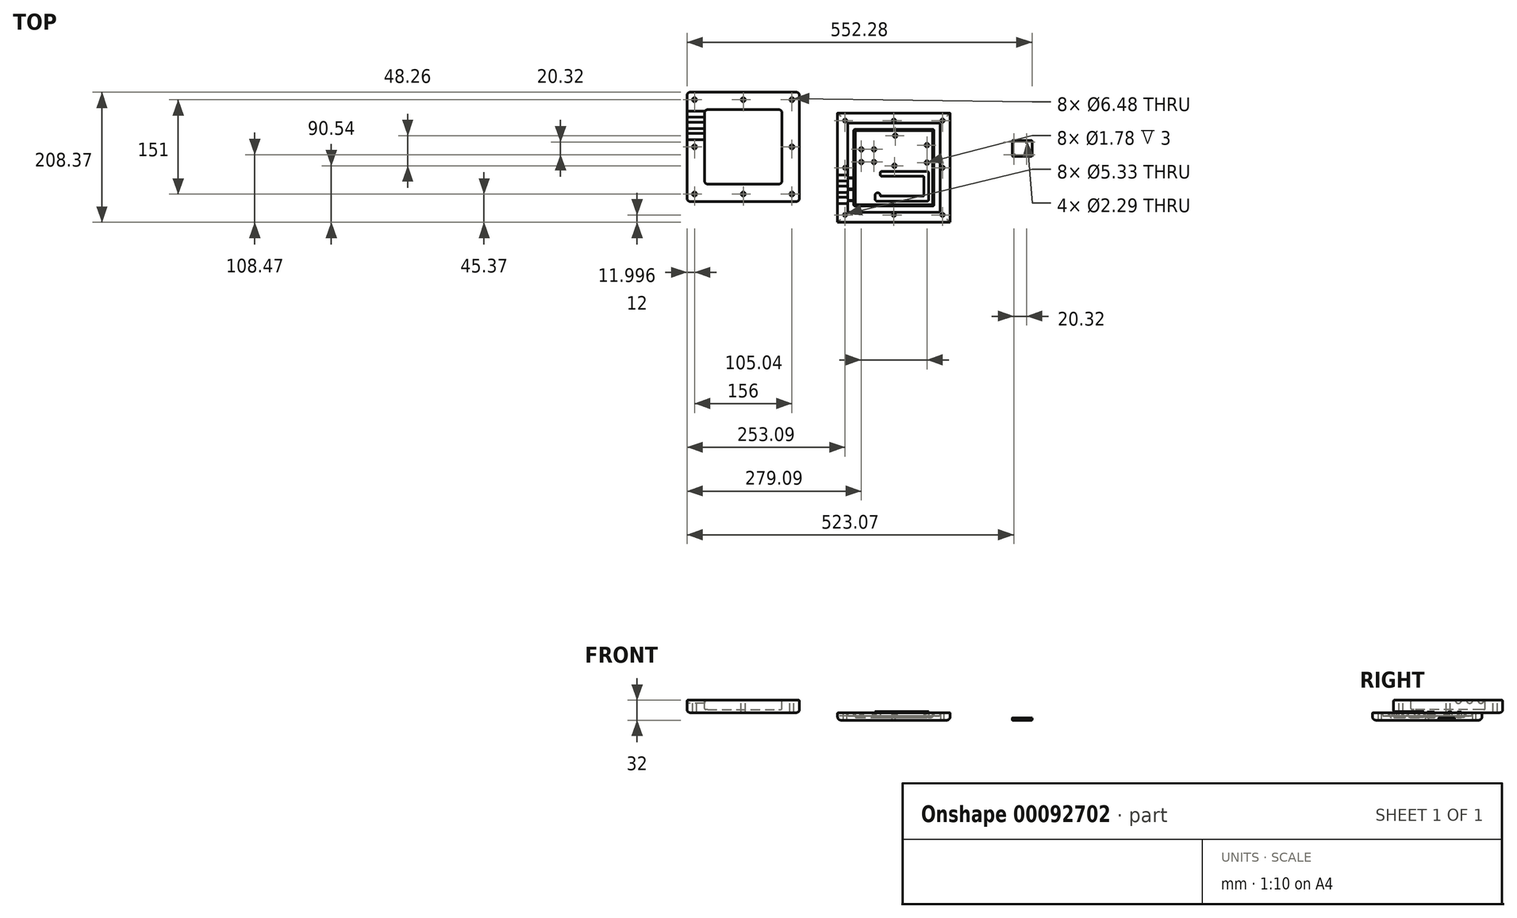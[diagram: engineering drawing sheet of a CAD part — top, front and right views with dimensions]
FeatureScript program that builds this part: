
annotation { "Feature Type Name" : "Feature", "Feature Type Description" : "" }
export const myFeature = defineFeature(function(context is Context, id is Id, definition is map)
    precondition{}
    {
        {
            var Q0;
            Q0=qCreatedBy(makeId("Top.planeOp"),FACE);
            var sketch = newSketch(context, id + "F0", { "sketchPlane" : qUnion([Q0])});
            skLineSegment(sketch, "E0.bottom", {"start": v(-90, 87.5) * mm, "end": v(90, 87.5) * mm});
            skLineSegment(sketch, "E0.top", {"start": v(-90, -87.5) * mm, "end": v(90, -87.5) * mm});
            skLineSegment(sketch, "E0.left", {"start": v(-90, 87.5) * mm, "end": v(-90, -87.5) * mm});
            skLineSegment(sketch, "E0.right", {"start": v(90, 87.5) * mm, "end": v(90, -87.5) * mm});
            skLineSegment(sketch, "E1", {"start": v(0, 87.5) * mm, "end": v(0, 0) * mm});
            skLineSegment(sketch, "E2", {"start": v(0, 0) * mm, "end": v(-90, 0) * mm});
            skSolve(sketch);
        }
        {
            var Q0;
            Q0 = qSketchRegion(id + "F0", true);
            extrude(context, id + "F1", {"entities" : qUnion([Q0]), "depth" : 12 * mm});
        }
        {
            var Q0;
            Q0=makeQuery(id+"F1.opExtrude","CAP_EDGE",EDGE,{"disambiguationData":[OSD([sQuery(id+"F0.wireOp",EDGE,"E0.top")])],"isStart":true});
            var Q1;
            Q1=makeQuery(id+"F1.opExtrude","CAP_EDGE",EDGE,{"disambiguationData":[OSD([sQuery(id+"F0.wireOp",EDGE,"E0.left")])],"isStart":true});
            var Q2;
            Q2=makeQuery(id+"F1.opExtrude","CAP_EDGE",EDGE,{"disambiguationData":[OSD([sQuery(id+"F0.wireOp",EDGE,"E0.bottom")])],"isStart":true});
            var Q3;
            Q3=makeQuery(id+"F1.opExtrude","CAP_EDGE",EDGE,{"disambiguationData":[OSD([sQuery(id+"F0.wireOp",EDGE,"E0.right")])],"isStart":true});
            fillet(context, id + "F2", {"entities" : qUnion([Q0, Q1, Q2, Q3]), "radius" : 5 * mm, "tangentPropagation" : true, "allowEdgeOverflow" : false});
        }
        {
            var Q0;
            Q0=makeQuery(id+"F1.opExtrude","CAP_FACE",FACE,{"disambiguationData":[OSD([sQuery(id+"F0.wireOp",EDGE,"E0.bottom"),sQuery(id+"F0.wireOp",EDGE,"E0.top"),sQuery(id+"F0.wireOp",EDGE,"E0.left"),sQuery(id+"F0.wireOp",EDGE,"E0.right")])],"isStart":false});
            var sketch = newSketch(context, id + "F3", { "sketchPlane" : qUnion([Q0])});
            skLineSegment(sketch, "E3.bottom", {"start": v(-62, 59.5) * mm, "end": v(62, 59.5) * mm});
            skLineSegment(sketch, "E3.top", {"start": v(-62, -59.5) * mm, "end": v(62, -59.5) * mm});
            skLineSegment(sketch, "E3.left", {"start": v(-62, 59.5) * mm, "end": v(-62, -59.5) * mm});
            skLineSegment(sketch, "E3.right", {"start": v(62, 59.5) * mm, "end": v(62, -59.5) * mm});
            skLineSegment(sketch, "E4", {"start": v(0, 59.5) * mm, "end": v(0, 0) * mm});
            skLineSegment(sketch, "E5", {"start": v(0, 0) * mm, "end": v(-62, 0) * mm});
            skSolve(sketch);
        }
        {
            var Q0;
            Q0 = qSketchRegion(id + "F3", true);
            extrude(context, id + "F4", {"entities" : qUnion([Q0]), "operationType" : NewBodyOperationType.REMOVE, "oppositeDirection" : true, "depth" : 8 * mm});
        }
        {
            var Q0;
            Q0=makeQuery(id+"F4.boolean.opBoolean","COPY",EDGE,{"derivedFrom":makeQuery(id+"F4.opExtrude","CAP_EDGE",EDGE,{"disambiguationData":[OSD([sQuery(id+"F3.wireOp",EDGE,"E3.bottom")])],"isStart":false})});
            var Q1;
            Q1=makeQuery(id+"F4.boolean.opBoolean","COPY",EDGE,{"derivedFrom":makeQuery(id+"F4.opExtrude","CAP_EDGE",EDGE,{"disambiguationData":[OSD([sQuery(id+"F3.wireOp",EDGE,"E3.right")])],"isStart":false})});
            var Q2;
            Q2=makeQuery(id+"F4.boolean.opBoolean","COPY",EDGE,{"derivedFrom":makeQuery(id+"F4.opExtrude","CAP_EDGE",EDGE,{"disambiguationData":[OSD([sQuery(id+"F3.wireOp",EDGE,"E3.top")])],"isStart":false})});
            var Q3;
            Q3=makeQuery(id+"F4.boolean.opBoolean","COPY",EDGE,{"derivedFrom":makeQuery(id+"F4.opExtrude","CAP_EDGE",EDGE,{"disambiguationData":[OSD([sQuery(id+"F3.wireOp",EDGE,"E3.left")])],"isStart":false})});
            fillet(context, id + "F5", {"entities" : qUnion([Q0, Q1, Q2, Q3]), "radius" : 2 * mm, "tangentPropagation" : true, "allowEdgeOverflow" : false});
        }
        {
            var Q0;
            Q0=makeQuery(id+"F1.opExtrude","CAP_EDGE",EDGE,{"disambiguationData":[OSD([sQuery(id+"F0.wireOp",EDGE,"E0.top")])],"isStart":false});
            var Q1;
            Q1=makeQuery(id+"F1.opExtrude","CAP_EDGE",EDGE,{"disambiguationData":[OSD([sQuery(id+"F0.wireOp",EDGE,"E0.left")])],"isStart":false});
            var Q2;
            Q2=makeQuery(id+"F1.opExtrude","CAP_EDGE",EDGE,{"disambiguationData":[OSD([sQuery(id+"F0.wireOp",EDGE,"E0.bottom")])],"isStart":false});
            var Q3;
            Q3=makeQuery(id+"F1.opExtrude","CAP_EDGE",EDGE,{"disambiguationData":[OSD([sQuery(id+"F0.wireOp",EDGE,"E0.right")])],"isStart":false});
            fillet(context, id + "F6", {"entities" : qUnion([Q0, Q1, Q2, Q3]), "radius" : 1 * mm, "tangentPropagation" : true, "allowEdgeOverflow" : false});
        }
        {
            var Q0;
            Q0=makeQuery(id+"F1.opExtrude","CAP_FACE",FACE,{"disambiguationData":[OSD([sQuery(id+"F0.wireOp",EDGE,"E0.bottom"),sQuery(id+"F0.wireOp",EDGE,"E0.top"),sQuery(id+"F0.wireOp",EDGE,"E0.left"),sQuery(id+"F0.wireOp",EDGE,"E0.right")])],"isStart":false});
            var sketch = newSketch(context, id + "F7", { "sketchPlane" : qUnion([Q0])});
            skLineSegment(sketch, "E6.bottom", {"start": v(-64, 61.5) * mm, "end": v(64, 61.5) * mm});
            skLineSegment(sketch, "E6.top", {"start": v(-64, -61.5) * mm, "end": v(64, -61.5) * mm});
            skLineSegment(sketch, "E6.left", {"start": v(-64, 61.5) * mm, "end": v(-64, -61.5) * mm});
            skLineSegment(sketch, "E6.right", {"start": v(64, 61.5) * mm, "end": v(64, -61.5) * mm});
            skLineSegment(sketch, "E7", {"start": v(-64, 0) * mm, "end": v(0, 0) * mm, "construction": true});
            skLineSegment(sketch, "E8", {"start": v(0, 0) * mm, "end": v(0, 61.5) * mm, "construction": true});
            skLineSegment(sketch, "E9.bottom", {"start": v(-74, 71.5) * mm, "end": v(74, 71.5) * mm});
            skLineSegment(sketch, "E9.top", {"start": v(-74, -71.5) * mm, "end": v(74, -71.5) * mm});
            skLineSegment(sketch, "E9.left", {"start": v(-74, 71.5) * mm, "end": v(-74, -71.5) * mm});
            skLineSegment(sketch, "E9.right", {"start": v(74, 71.5) * mm, "end": v(74, -71.5) * mm});
            skLineSegment(sketch, "E10", {"start": v(0, 61.5) * mm, "end": v(0, 71.5) * mm, "construction": true});
            skPoint(sketch, "E10.startSnap0", {"position": v(0, 71.5) * mm});
            skLineSegment(sketch, "E11", {"start": v(-64, 0) * mm, "end": v(-74, 0) * mm, "construction": true});
            skSolve(sketch);
        }
        {
            var Q0;
            Q0=makeQuery(id+"F7.imprint","IMPRINT",FACE,{"disambiguationData":[TD([[makeQuery(id+"F7.imprint","IMPRINT",EDGE,{"derivedFrom":sQuery(id+"F7.wireOp",EDGE,"E6.bottom")}),1.0]])]});
            extrude(context, id + "F8", {"entities" : qUnion([Q0]), "operationType" : NewBodyOperationType.REMOVE, "oppositeDirection" : true, "depth" : 5 * mm});
        }
        {
            var Q0;
            Q0=makeQuery(id+"F8.boolean.opBoolean","COPY",EDGE,{"derivedFrom":makeQuery(id+"F8.opExtrude","SWEPT_EDGE",EDGE,{"disambiguationData":[OSD([sQuery(id+"F7.wireOp",EDGE,"E9.bottom"),sQuery(id+"F7.wireOp",EDGE,"E9.left")])]})});
            var Q1;
            Q1=makeQuery(id+"F8.boolean.opBoolean","COPY",EDGE,{"derivedFrom":makeQuery(id+"F8.opExtrude","SWEPT_EDGE",EDGE,{"disambiguationData":[OSD([sQuery(id+"F7.wireOp",EDGE,"E9.bottom"),sQuery(id+"F7.wireOp",EDGE,"E9.right")])]})});
            var Q2;
            Q2=makeQuery(id+"F8.boolean.opBoolean","COPY",EDGE,{"derivedFrom":makeQuery(id+"F8.opExtrude","SWEPT_EDGE",EDGE,{"disambiguationData":[OSD([sQuery(id+"F7.wireOp",EDGE,"E9.top"),sQuery(id+"F7.wireOp",EDGE,"E9.right")])]})});
            var Q3;
            Q3=makeQuery(id+"F8.boolean.opBoolean","COPY",EDGE,{"derivedFrom":makeQuery(id+"F8.opExtrude","SWEPT_EDGE",EDGE,{"disambiguationData":[OSD([sQuery(id+"F7.wireOp",EDGE,"E9.top"),sQuery(id+"F7.wireOp",EDGE,"E9.left")])]})});
            var Q4;
            Q4=makeQuery(id+"F8.boolean.opBoolean","COPY",EDGE,{"derivedFrom":makeQuery(id+"F8.opExtrude","SWEPT_EDGE",EDGE,{"disambiguationData":[OSD([sQuery(id+"F7.wireOp",EDGE,"E6.bottom"),sQuery(id+"F7.wireOp",EDGE,"E6.right")])]})});
            var Q5;
            Q5=makeQuery(id+"F8.boolean.opBoolean","COPY",EDGE,{"derivedFrom":makeQuery(id+"F8.opExtrude","SWEPT_EDGE",EDGE,{"disambiguationData":[OSD([sQuery(id+"F7.wireOp",EDGE,"E6.bottom"),sQuery(id+"F7.wireOp",EDGE,"E6.left")])]})});
            var Q6;
            Q6=makeQuery(id+"F8.boolean.opBoolean","COPY",EDGE,{"derivedFrom":makeQuery(id+"F8.opExtrude","SWEPT_EDGE",EDGE,{"disambiguationData":[OSD([sQuery(id+"F7.wireOp",EDGE,"E6.top"),sQuery(id+"F7.wireOp",EDGE,"E6.left")])]})});
            var Q7;
            Q7=makeQuery(id+"F8.boolean.opBoolean","COPY",EDGE,{"derivedFrom":makeQuery(id+"F8.opExtrude","SWEPT_EDGE",EDGE,{"disambiguationData":[OSD([sQuery(id+"F7.wireOp",EDGE,"E6.top"),sQuery(id+"F7.wireOp",EDGE,"E6.right")])]})});
            fillet(context, id + "F9", {"entities" : qUnion([Q0, Q1, Q2, Q3, Q4, Q5, Q6, Q7]), "radius" : 2 * mm, "tangentPropagation" : true, "allowEdgeOverflow" : false});
        }
        {
            var Q0;
            Q0=makeQuery(id+"F8.boolean.opBoolean","COPY",EDGE,{"derivedFrom":makeQuery(id+"F8.opExtrude","CAP_EDGE",EDGE,{"disambiguationData":[OSD([sQuery(id+"F7.wireOp",EDGE,"E9.bottom")])],"isStart":false})});
            var Q1;
            Q1=makeQuery(id+"F8.boolean.opBoolean","COPY",EDGE,{"derivedFrom":makeQuery(id+"F8.opExtrude","CAP_EDGE",EDGE,{"disambiguationData":[OSD([sQuery(id+"F7.wireOp",EDGE,"E6.right")])],"isStart":false})});
            fillet(context, id + "F10", {"entities" : qUnion([Q0, Q1]), "radius" : 2 * mm, "tangentPropagation" : true, "allowEdgeOverflow" : false});
        }
        {
            var Q0;
            Q0=makeQuery(id+"F8.boolean.opBoolean","COPY",FACE,{"derivedFrom":makeQuery(id+"F8.opExtrude","CAP_FACE",FACE,{"disambiguationData":[OSD([sQuery(id+"F7.wireOp",EDGE,"E6.bottom"),sQuery(id+"F7.wireOp",EDGE,"E6.top"),sQuery(id+"F7.wireOp",EDGE,"E6.left"),sQuery(id+"F7.wireOp",EDGE,"E6.right"),sQuery(id+"F7.wireOp",EDGE,"E9.bottom"),sQuery(id+"F7.wireOp",EDGE,"E9.top"),sQuery(id+"F7.wireOp",EDGE,"E9.left"),sQuery(id+"F7.wireOp",EDGE,"E9.right")])],"isStart":false})});
            var sketch = newSketch(context, id + "F11", { "sketchPlane" : qUnion([Q0])});
            skLineSegment(sketch, "E12.bottom", {"start": v(-71.5, 71) * mm, "end": v(71.5, 71) * mm});
            skLineSegment(sketch, "E12.top", {"start": v(-71.5, -71) * mm, "end": v(71.5, -71) * mm});
            skLineSegment(sketch, "E12.left", {"start": v(-73.5, 69) * mm, "end": v(-73.5, -69) * mm});
            skLineSegment(sketch, "E12.right", {"start": v(73.5, 69) * mm, "end": v(73.5, -69) * mm});
            skLineSegment(sketch, "E13.bottom", {"start": v(-62.37, 61.87) * mm, "end": v(62.37, 61.87) * mm});
            skLineSegment(sketch, "E13.top", {"start": v(-62.37, -61.87) * mm, "end": v(62.37, -61.87) * mm});
            skLineSegment(sketch, "E13.left", {"start": v(-64.37, 59.87) * mm, "end": v(-64.37, -59.87) * mm});
            skLineSegment(sketch, "E13.right", {"start": v(64.37, 59.87) * mm, "end": v(64.37, -59.87) * mm});
            skLineSegment(sketch, "E14", {"start": v(0, 61.87) * mm, "end": v(0, 71) * mm, "construction": true});
            skLineSegment(sketch, "E15", {"start": v(-64.37, 0) * mm, "end": v(-73.5, 0) * mm, "construction": true});
            skPoint(sketch, "E16", {"position": v(-72, 0) * mm});
            skPoint(sketch, "E17.visualSharp", {"position": v(-73.5, 71) * mm});
            skArc(sketch, "E17.filletArc", {"start": v(-71.5, 71) * mm, "mid": v(-72.91, 70.41) * mm, "end": v(-73.5, 69) * mm});
            skPoint(sketch, "E18.visualSharp", {"position": v(73.5, 71) * mm});
            skArc(sketch, "E18.filletArc", {"start": v(73.5, 69) * mm, "mid": v(72.91, 70.41) * mm, "end": v(71.5, 71) * mm});
            skPoint(sketch, "E19.visualSharp", {"position": v(73.5, -71) * mm});
            skArc(sketch, "E19.filletArc", {"start": v(71.5, -71) * mm, "mid": v(72.91, -70.41) * mm, "end": v(73.5, -69) * mm});
            skPoint(sketch, "E20.visualSharp", {"position": v(-73.5, -71) * mm});
            skArc(sketch, "E20.filletArc", {"start": v(-73.5, -69) * mm, "mid": v(-72.91, -70.41) * mm, "end": v(-71.5, -71) * mm});
            skPoint(sketch, "E21.visualSharp", {"position": v(-64.37, -61.87) * mm});
            skArc(sketch, "E21.filletArc", {"start": v(-64.37, -59.87) * mm, "mid": v(-63.79, -61.29) * mm, "end": v(-62.37, -61.87) * mm});
            skPoint(sketch, "E22.visualSharp", {"position": v(64.37, -61.87) * mm});
            skArc(sketch, "E22.filletArc", {"start": v(62.37, -61.87) * mm, "mid": v(63.79, -61.29) * mm, "end": v(64.37, -59.87) * mm});
            skPoint(sketch, "E23.visualSharp", {"position": v(64.37, 61.87) * mm});
            skArc(sketch, "E23.filletArc", {"start": v(64.37, 59.87) * mm, "mid": v(63.79, 61.29) * mm, "end": v(62.37, 61.87) * mm});
            skPoint(sketch, "E24.visualSharp", {"position": v(-64.37, 61.87) * mm});
            skArc(sketch, "E24.filletArc", {"start": v(-62.37, 61.87) * mm, "mid": v(-63.79, 61.29) * mm, "end": v(-64.37, 59.87) * mm});
            skSolve(sketch);
        }
        {
            var Q0;
            Q0 = qSketchRegion(id + "F11", true);
            extrude(context, id + "F12", {"entities" : qUnion([Q0]), "depth" : 5 / 406.4 * mm});
        }
        {
            var Q0;
            Q0=makeQuery(id+"F12.opExtrude","CAP_EDGE",EDGE,{"disambiguationData":[OSD([sQuery(id+"F11.wireOp",EDGE,"E12.left")])],"isStart":false});
            var Q1;
            Q1=makeQuery(id+"F12.opExtrude","CAP_EDGE",EDGE,{"disambiguationData":[OSD([sQuery(id+"F11.wireOp",EDGE,"E13.left")])],"isStart":false});
            fillet(context, id + "F13", {"entities" : qUnion([Q0, Q1]), "radius" : 4 * mm, "tangentPropagation" : true, "allowEdgeOverflow" : false});
        }
        {
            var Q0;
            Q0=makeQuery(id+"F4.boolean.opBoolean","COPY",FACE,{"derivedFrom":makeQuery(id+"F4.opExtrude","CAP_FACE",FACE,{"disambiguationData":[OSD([sQuery(id+"F3.wireOp",EDGE,"E3.bottom"),sQuery(id+"F3.wireOp",EDGE,"E3.top"),sQuery(id+"F3.wireOp",EDGE,"E3.left"),sQuery(id+"F3.wireOp",EDGE,"E3.right")])],"isStart":false})});
            var sketch = newSketch(context, id + "F14", { "sketchPlane" : qUnion([Q0])});
            skLineSegment(sketch, "E25.bottom", {"start": v(-13, 53.5) * mm, "end": v(56, 53.5) * mm, "construction": true});
            skLineSegment(sketch, "E25.top", {"start": v(-13, 0.5) * mm, "end": v(56, 0.5) * mm, "construction": true});
            skLineSegment(sketch, "E25.left", {"start": v(-13, 53.5) * mm, "end": v(-13, 0.5) * mm, "construction": true});
            skLineSegment(sketch, "E25.right", {"start": v(56, 53.5) * mm, "end": v(56, 0.5) * mm, "construction": true});
            skCircle(sketch, "E26", {"center": v(0.97, 3.04) * mm, "radius": 3 * mm});
            skCircle(sketch, "E27", {"center": v(2.24, 51.3) * mm, "radius": 3 * mm});
            skCircle(sketch, "E28", {"center": v(53.04, 36.06) * mm, "radius": 3 * mm});
            skCircle(sketch, "E29", {"center": v(53.04, 8.12) * mm, "radius": 3 * mm});
            skSolve(sketch);
        }
        {
            var Q0;
            Q0 = qSketchRegion(id + "F14", true);
            extrude(context, id + "F15", {"entities" : qUnion([Q0]), "operationType" : NewBodyOperationType.ADD, "depth" : 9 * mm});
        }
        {
            var Q0;
            Q0=makeQuery(id+"F15.opExtrude","CAP_FACE",FACE,{"disambiguationData":[OSD([sQuery(id+"F14.wireOp",EDGE,"E27")])],"isStart":false});
            var sketch = newSketch(context, id + "F16", { "sketchPlane" : qUnion([Q0])});
            skCircle(sketch, "E30", {"center": v(2.24, 51.3) * mm, "radius": 0.89 * mm});
            skCircle(sketch, "E31", {"center": v(53.04, 36.06) * mm, "radius": 0.89 * mm});
            skCircle(sketch, "E32", {"center": v(53.04, 8.12) * mm, "radius": 0.89 * mm});
            skCircle(sketch, "E33", {"center": v(0.97, 3.04) * mm, "radius": 0.89 * mm});
            skSolve(sketch);
        }
        {
            var Q0;
            Q0 = qSketchRegion(id + "F16", true);
            extrude(context, id + "F17", {"entities" : qUnion([Q0]), "operationType" : NewBodyOperationType.REMOVE, "oppositeDirection" : true, "depth" : 3 * mm});
        }
        {
            var Q0;
            Q0=makeQuery(id+"F4.boolean.opBoolean","COPY",FACE,{"derivedFrom":makeQuery(id+"F4.opExtrude","CAP_FACE",FACE,{"disambiguationData":[OSD([sQuery(id+"F3.wireOp",EDGE,"E3.bottom"),sQuery(id+"F3.wireOp",EDGE,"E3.top"),sQuery(id+"F3.wireOp",EDGE,"E3.left"),sQuery(id+"F3.wireOp",EDGE,"E3.right")])],"isStart":false})});
            var sketch = newSketch(context, id + "F18", { "sketchPlane" : qUnion([Q0])});
            skLineSegment(sketch, "E34", {"start": v(-21.85, -5.75) * mm, "end": v(-21.85, -13.75) * mm});
            skLineSegment(sketch, "E35", {"start": v(-21.85, -13.75) * mm, "end": v(48, -13.75) * mm});
            skLineSegment(sketch, "E36", {"start": v(48, -13.75) * mm, "end": v(48, -45.5) * mm});
            skLineSegment(sketch, "E37", {"start": v(48, -45.5) * mm, "end": v(-21.85, -45.5) * mm});
            skLineSegment(sketch, "E38", {"start": v(-21.85, -45.5) * mm, "end": v(-21.85, -40.5) * mm});
            skLineSegment(sketch, "E39", {"start": v(-21.85, -40.5) * mm, "end": v(-29.85, -40.5) * mm});
            skLineSegment(sketch, "E40", {"start": v(-29.85, -40.5) * mm, "end": v(-29.85, -53.5) * mm});
            skLineSegment(sketch, "E41", {"start": v(-29.85, -53.5) * mm, "end": v(56, -53.5) * mm});
            skLineSegment(sketch, "E42", {"start": v(56, -53.5) * mm, "end": v(56, -5.75) * mm});
            skLineSegment(sketch, "E43", {"start": v(56, -5.75) * mm, "end": v(-21.85, -5.75) * mm});
            skSolve(sketch);
        }
        {
            var Q0;
            Q0 = qSketchRegion(id + "F18", true);
            extrude(context, id + "F19", {"entities" : qUnion([Q0]), "operationType" : NewBodyOperationType.ADD, "depth" : 10 * mm});
        }
        {
            var Q0;
            Q0=makeQuery(id+"F19.opExtrude","SWEPT_EDGE",EDGE,{"disambiguationData":[OSD([sQuery(id+"F18.wireOp",EDGE,"E40"),sQuery(id+"F18.wireOp",EDGE,"E41")])]});
            var Q1;
            Q1=makeQuery(id+"F19.opExtrude","SWEPT_EDGE",EDGE,{"disambiguationData":[OSD([sQuery(id+"F18.wireOp",EDGE,"E39"),sQuery(id+"F18.wireOp",EDGE,"E40")])]});
            var Q2;
            Q2=makeQuery(id+"F19.opExtrude","SWEPT_EDGE",EDGE,{"disambiguationData":[OSD([sQuery(id+"F18.wireOp",EDGE,"E38"),sQuery(id+"F18.wireOp",EDGE,"E39")])]});
            var Q3;
            Q3=makeQuery(id+"F19.opExtrude","SWEPT_EDGE",EDGE,{"disambiguationData":[OSD([sQuery(id+"F18.wireOp",EDGE,"E34"),sQuery(id+"F18.wireOp",EDGE,"E43")])]});
            var Q4;
            Q4=makeQuery(id+"F19.opExtrude","SWEPT_EDGE",EDGE,{"disambiguationData":[OSD([sQuery(id+"F18.wireOp",EDGE,"E42"),sQuery(id+"F18.wireOp",EDGE,"E43")])]});
            var Q5;
            Q5=makeQuery(id+"F19.opExtrude","SWEPT_EDGE",EDGE,{"disambiguationData":[OSD([sQuery(id+"F18.wireOp",EDGE,"E41"),sQuery(id+"F18.wireOp",EDGE,"E42")])]});
            var Q6;
            Q6=makeQuery(id+"F19.opExtrude","SWEPT_EDGE",EDGE,{"disambiguationData":[OSD([sQuery(id+"F18.wireOp",EDGE,"E34"),sQuery(id+"F18.wireOp",EDGE,"E35")])]});
            fillet(context, id + "F20", {"entities" : qUnion([Q0, Q1, Q2, Q3, Q4, Q5, Q6]), "radius" : 3 * mm, "tangentPropagation" : true, "allowEdgeOverflow" : false});
        }
        {
            var Q0;
            Q0=makeQuery(id+"F19.opExtrude","SWEPT_EDGE",EDGE,{"disambiguationData":[OSD([sQuery(id+"F18.wireOp",EDGE,"E37"),sQuery(id+"F18.wireOp",EDGE,"E38")])]});
            var Q1;
            Q1=makeQuery(id+"F19.opExtrude","SWEPT_EDGE",EDGE,{"disambiguationData":[OSD([sQuery(id+"F18.wireOp",EDGE,"E36"),sQuery(id+"F18.wireOp",EDGE,"E37")])]});
            var Q2;
            Q2=makeQuery(id+"F19.opExtrude","SWEPT_EDGE",EDGE,{"disambiguationData":[OSD([sQuery(id+"F18.wireOp",EDGE,"E35"),sQuery(id+"F18.wireOp",EDGE,"E36")])]});
            fillet(context, id + "F21", {"entities" : qUnion([Q0, Q1, Q2]), "radius" : 1 * mm, "tangentPropagation" : true, "allowEdgeOverflow" : false});
        }
        {
            var Q0;
            Q0=makeQuery(id+"F19.opExtrude","CAP_EDGE",EDGE,{"disambiguationData":[OSD([sQuery(id+"F18.wireOp",EDGE,"E41")])],"isStart":true});
            var Q1;
            Q1=makeQuery(id+"F19.opExtrude","CAP_EDGE",EDGE,{"disambiguationData":[OSD([sQuery(id+"F18.wireOp",EDGE,"E41")])],"isStart":false});
            fillet(context, id + "F22", {"entities" : qUnion([Q0, Q1]), "radius" : 1 * mm, "tangentPropagation" : true, "allowEdgeOverflow" : false});
        }
        {
            var Q0;
            Q0=qCreatedBy(makeId("Top.planeOp"),FACE);
            var sketch = newSketch(context, id + "F23", { "sketchPlane" : qUnion([Q0])});
            skLineSegment(sketch, "E44.bottom", {"start": v(189.44, 43.83) * mm, "end": v(221.19, 43.83) * mm});
            skLineSegment(sketch, "E44.top", {"start": v(189.44, 18.43) * mm, "end": v(221.19, 18.43) * mm});
            skLineSegment(sketch, "E44.left", {"start": v(189.44, 43.83) * mm, "end": v(189.44, 18.43) * mm});
            skLineSegment(sketch, "E44.right", {"start": v(221.19, 43.83) * mm, "end": v(221.19, 18.43) * mm});
            skCircle(sketch, "E45", {"center": v(191.98, 20.97) * mm, "radius": 1.14 * mm});
            skCircle(sketch, "E46", {"center": v(191.98, 41.3) * mm, "radius": 1.14 * mm});
            skCircle(sketch, "E47", {"center": v(212.3, 41.3) * mm, "radius": 1.14 * mm});
            skCircle(sketch, "E48", {"center": v(212.3, 20.97) * mm, "radius": 1.14 * mm});
            skSolve(sketch);
        }
        {
            var Q0;
            Q0 = qSketchRegion(id + "F23", true);
            extrude(context, id + "F24", {"entities" : qUnion([Q0]), "depth" : 3.75 * mm});
        }
        {
            var Q0;
            Q0=makeQuery(id+"F24.opExtrude","SWEPT_EDGE",EDGE,{"disambiguationData":[OSD([sQuery(id+"F23.wireOp",EDGE,"E44.top"),sQuery(id+"F23.wireOp",EDGE,"E44.left")])]});
            var Q1;
            Q1=makeQuery(id+"F24.opExtrude","SWEPT_EDGE",EDGE,{"disambiguationData":[OSD([sQuery(id+"F23.wireOp",EDGE,"E44.top"),sQuery(id+"F23.wireOp",EDGE,"E44.right")])]});
            var Q2;
            Q2=makeQuery(id+"F24.opExtrude","SWEPT_EDGE",EDGE,{"disambiguationData":[OSD([sQuery(id+"F23.wireOp",EDGE,"E44.bottom"),sQuery(id+"F23.wireOp",EDGE,"E44.right")])]});
            var Q3;
            Q3=makeQuery(id+"F24.opExtrude","SWEPT_EDGE",EDGE,{"disambiguationData":[OSD([sQuery(id+"F23.wireOp",EDGE,"E44.bottom"),sQuery(id+"F23.wireOp",EDGE,"E44.left")])]});
            fillet(context, id + "F25", {"entities" : qUnion([Q0, Q1, Q2, Q3]), "radius" : 1 * mm, "tangentPropagation" : true, "allowEdgeOverflow" : false});
        }
        {
            var Q0;
            Q0=makeQuery(id+"F24.opExtrude","CAP_EDGE",EDGE,{"disambiguationData":[OSD([sQuery(id+"F23.wireOp",EDGE,"E44.bottom")])],"isStart":false});
            var Q1;
            Q1=makeQuery(id+"F24.opExtrude","CAP_EDGE",EDGE,{"disambiguationData":[OSD([sQuery(id+"F23.wireOp",EDGE,"E44.bottom")])],"isStart":true});
            fillet(context, id + "F26", {"entities" : qUnion([Q0, Q1]), "radius" : 0.5 * mm, "tangentPropagation" : true, "allowEdgeOverflow" : false});
        }
        {
            var Q0;
            Q0=makeQuery(id+"F4.boolean.opBoolean","COPY",FACE,{"derivedFrom":makeQuery(id+"F4.opExtrude","CAP_FACE",FACE,{"disambiguationData":[OSD([sQuery(id+"F3.wireOp",EDGE,"E3.bottom"),sQuery(id+"F3.wireOp",EDGE,"E3.top"),sQuery(id+"F3.wireOp",EDGE,"E3.left"),sQuery(id+"F3.wireOp",EDGE,"E3.right")])],"isStart":false})});
            var sketch = newSketch(context, id + "F27", { "sketchPlane" : qUnion([Q0])});
            skCircle(sketch, "E49", {"center": v(-52, 29.5) * mm, "radius": 3 * mm});
            skCircle(sketch, "E50", {"center": v(-31.68, 29.5) * mm, "radius": 3 * mm});
            skCircle(sketch, "E51", {"center": v(-52, 9.18) * mm, "radius": 3 * mm});
            skCircle(sketch, "E52", {"center": v(-31.68, 9.18) * mm, "radius": 3 * mm});
            skSolve(sketch);
        }
        {
            var Q0;
            Q0 = qSketchRegion(id + "F27", true);
            extrude(context, id + "F28", {"entities" : qUnion([Q0]), "operationType" : NewBodyOperationType.ADD, "depth" : 6 * mm});
        }
        {
            var Q0;
            Q0=makeQuery(id+"F28.opExtrude","CAP_FACE",FACE,{"disambiguationData":[OSD([sQuery(id+"F27.wireOp",EDGE,"E49")])],"isStart":false});
            var sketch = newSketch(context, id + "F29", { "sketchPlane" : qUnion([Q0])});
            skCircle(sketch, "E53", {"center": v(-52, 29.5) * mm, "radius": 0.89 * mm});
            skCircle(sketch, "E54", {"center": v(-52, 9.18) * mm, "radius": 0.89 * mm});
            skCircle(sketch, "E55", {"center": v(-31.68, 9.18) * mm, "radius": 0.89 * mm});
            skCircle(sketch, "E56", {"center": v(-31.68, 29.5) * mm, "radius": 0.89 * mm});
            skSolve(sketch);
        }
        {
            var Q0;
            Q0 = qSketchRegion(id + "F29", true);
            extrude(context, id + "F30", {"entities" : qUnion([Q0]), "operationType" : NewBodyOperationType.REMOVE, "oppositeDirection" : true, "depth" : 3 * mm});
        }
        {
            var Q0;
            {var subQ0=sQuery(id+"F0.wireOp",EDGE,"E0.right");var subQ1=sQuery(id+"F0.wireOp",EDGE,"E0.left");var subQ2=sQuery(id+"F0.wireOp",EDGE,"E0.top");var subQ3=sQuery(id+"F0.wireOp",EDGE,"E0.bottom");Q0=makeQuery(id+"F8.boolean.opBoolean","SPLIT",FACE,{"disambiguationData":[TD([makeQuery(id+"F6.opFillet","BLEND_FACE",FACE,{"disambiguationData":[OSD([subQ3])]})])],"derivedFrom":makeQuery(id+"F1.opExtrude","CAP_FACE",FACE,{"disambiguationData":[OSD([subQ3,subQ2,subQ1,subQ0])],"isStart":false})});}
            var sketch = newSketch(context, id + "F31", { "sketchPlane" : qUnion([Q0])});
            skLineSegment(sketch, "E57.bottom", {"start": v(-78, 75.5) * mm, "end": v(78, 75.5) * mm, "construction": true});
            skLineSegment(sketch, "E57.top", {"start": v(-78, -75.5) * mm, "end": v(78, -75.5) * mm, "construction": true});
            skLineSegment(sketch, "E57.left", {"start": v(-78, 75.5) * mm, "end": v(-78, -75.5) * mm, "construction": true});
            skLineSegment(sketch, "E57.right", {"start": v(78, 75.5) * mm, "end": v(78, -75.5) * mm, "construction": true});
            skLineSegment(sketch, "E58", {"start": v(0, 75.5) * mm, "end": v(0, 86.5) * mm, "construction": true});
            skLineSegment(sketch, "E59", {"start": v(-78, 0) * mm, "end": v(-89, 0) * mm, "construction": true});
            skCircle(sketch, "E60", {"center": v(-78, 75.5) * mm, "radius": 2.67 * mm});
            skCircle(sketch, "E61", {"center": v(-78, -75.5) * mm, "radius": 2.67 * mm});
            skCircle(sketch, "E62", {"center": v(78, -75.5) * mm, "radius": 2.67 * mm});
            skCircle(sketch, "E63", {"center": v(78, 0) * mm, "radius": 2.67 * mm});
            skCircle(sketch, "E64", {"center": v(0, 75.5) * mm, "radius": 2.67 * mm});
            skCircle(sketch, "E65", {"center": v(-78, 0) * mm, "radius": 2.67 * mm});
            skCircle(sketch, "E66", {"center": v(0, -75.5) * mm, "radius": 2.67 * mm});
            skCircle(sketch, "E67", {"center": v(78, 75.5) * mm, "radius": 2.67 * mm});
            skSolve(sketch);
        }
        {
            var Q0;
            Q0 = qSketchRegion(id + "F31", true);
            extrude(context, id + "F32", {"entities" : qUnion([Q0]), "operationType" : NewBodyOperationType.REMOVE, "endBound" : BoundingType.THROUGH_ALL, "oppositeDirection" : true, "depth" : 8 * mm});
        }
        {
            var Q0;
            {var subQ0=sQuery(id+"F0.wireOp",EDGE,"E0.right");var subQ1=sQuery(id+"F0.wireOp",EDGE,"E0.left");var subQ2=sQuery(id+"F0.wireOp",EDGE,"E0.top");var subQ3=sQuery(id+"F0.wireOp",EDGE,"E0.bottom");Q0=makeQuery(id+"F8.boolean.opBoolean","SPLIT",FACE,{"disambiguationData":[TD([makeQuery(id+"F6.opFillet","BLEND_FACE",FACE,{"disambiguationData":[OSD([subQ3])]})])],"derivedFrom":makeQuery(id+"F1.opExtrude","CAP_FACE",FACE,{"disambiguationData":[OSD([subQ3,subQ2,subQ1,subQ0])],"isStart":false})});}
            var sketch = newSketch(context, id + "F33", { "sketchPlane" : qUnion([Q0])});
            skLineSegment(sketch, "E68.bottom", {"start": v(-331.1, 120.87) * mm, "end": v(-151.1, 120.87) * mm});
            skLineSegment(sketch, "E68.top", {"start": v(-331.1, -54.13) * mm, "end": v(-151.1, -54.13) * mm});
            skLineSegment(sketch, "E68.left", {"start": v(-331.1, 120.87) * mm, "end": v(-331.1, -54.13) * mm});
            skLineSegment(sketch, "E68.right", {"start": v(-151.1, 120.87) * mm, "end": v(-151.1, -54.13) * mm});
            skSolve(sketch);
        }
        {
            var Q0;
            Q0 = qSketchRegion(id + "F33", true);
            extrude(context, id + "F34", {"entities" : qUnion([Q0]), "depth" : 20 * mm});
        }
        {
            var Q0;
            Q0=makeQuery(id+"F34.opExtrude","CAP_FACE",FACE,{"disambiguationData":[OSD([sQuery(id+"F33.wireOp",EDGE,"E68.bottom"),sQuery(id+"F33.wireOp",EDGE,"E68.top"),sQuery(id+"F33.wireOp",EDGE,"E68.left"),sQuery(id+"F33.wireOp",EDGE,"E68.right")])],"isStart":false});
            var sketch = newSketch(context, id + "F35", { "sketchPlane" : qUnion([Q0])});
            skLineSegment(sketch, "E69.bottom", {"start": v(-303.1, 92.87) * mm, "end": v(-179.1, 92.87) * mm});
            skLineSegment(sketch, "E69.top", {"start": v(-303.1, -26.13) * mm, "end": v(-179.1, -26.13) * mm});
            skLineSegment(sketch, "E69.left", {"start": v(-303.1, 92.87) * mm, "end": v(-303.1, -26.13) * mm});
            skLineSegment(sketch, "E69.right", {"start": v(-179.1, 92.87) * mm, "end": v(-179.1, -26.13) * mm});
            skLineSegment(sketch, "E70", {"start": v(-241.1, 92.87) * mm, "end": v(-241.1, 120.87) * mm});
            skLineSegment(sketch, "E71", {"start": v(-179.1, 33.37) * mm, "end": v(-151.1, 33.37) * mm});
            skSolve(sketch);
        }
        {
            var Q0;
            Q0 = qSketchRegion(id + "F35", true);
            extrude(context, id + "F36", {"entities" : qUnion([Q0]), "operationType" : NewBodyOperationType.REMOVE, "oppositeDirection" : true, "depth" : 15 * mm});
        }
        {
            var Q0;
            Q0=makeQuery(id+"F36.boolean.opBoolean","COPY",EDGE,{"derivedFrom":makeQuery(id+"F36.opExtrude","SWEPT_EDGE",EDGE,{"disambiguationData":[OSD([sQuery(id+"F35.wireOp",EDGE,"E69.bottom"),sQuery(id+"F35.wireOp",EDGE,"E69.left")])]})});
            var Q1;
            Q1=makeQuery(id+"F36.boolean.opBoolean","COPY",EDGE,{"derivedFrom":makeQuery(id+"F36.opExtrude","SWEPT_EDGE",EDGE,{"disambiguationData":[OSD([sQuery(id+"F35.wireOp",EDGE,"E69.bottom"),sQuery(id+"F35.wireOp",EDGE,"E69.right")])]})});
            var Q2;
            Q2=makeQuery(id+"F36.boolean.opBoolean","COPY",EDGE,{"derivedFrom":makeQuery(id+"F36.opExtrude","SWEPT_EDGE",EDGE,{"disambiguationData":[OSD([sQuery(id+"F35.wireOp",EDGE,"E69.top"),sQuery(id+"F35.wireOp",EDGE,"E69.left")])]})});
            var Q3;
            Q3=makeQuery(id+"F36.boolean.opBoolean","COPY",EDGE,{"derivedFrom":makeQuery(id+"F36.opExtrude","SWEPT_EDGE",EDGE,{"disambiguationData":[OSD([sQuery(id+"F35.wireOp",EDGE,"E69.top"),sQuery(id+"F35.wireOp",EDGE,"E69.right")])]})});
            fillet(context, id + "F37", {"entities" : qUnion([Q0, Q1, Q2, Q3]), "radius" : 5 * mm, "tangentPropagation" : true, "allowEdgeOverflow" : false});
        }
        {
            var Q0;
            Q0=makeQuery(id+"F34.opExtrude","SWEPT_EDGE",EDGE,{"disambiguationData":[OSD([sQuery(id+"F33.wireOp",EDGE,"E68.top"),sQuery(id+"F33.wireOp",EDGE,"E68.right")])]});
            var Q1;
            Q1=makeQuery(id+"F34.opExtrude","SWEPT_EDGE",EDGE,{"disambiguationData":[OSD([sQuery(id+"F33.wireOp",EDGE,"E68.top"),sQuery(id+"F33.wireOp",EDGE,"E68.left")])]});
            var Q2;
            Q2=makeQuery(id+"F34.opExtrude","SWEPT_EDGE",EDGE,{"disambiguationData":[OSD([sQuery(id+"F33.wireOp",EDGE,"E68.bottom"),sQuery(id+"F33.wireOp",EDGE,"E68.left")])]});
            var Q3;
            Q3=makeQuery(id+"F34.opExtrude","SWEPT_EDGE",EDGE,{"disambiguationData":[OSD([sQuery(id+"F33.wireOp",EDGE,"E68.bottom"),sQuery(id+"F33.wireOp",EDGE,"E68.right")])]});
            fillet(context, id + "F38", {"entities" : qUnion([Q0, Q1, Q2, Q3]), "radius" : 5 * mm, "tangentPropagation" : true, "allowEdgeOverflow" : false});
        }
        {
            var Q0;
            Q0=makeQuery(id+"F34.opExtrude","CAP_EDGE",EDGE,{"disambiguationData":[OSD([sQuery(id+"F33.wireOp",EDGE,"E68.bottom")])],"isStart":true});
            fillet(context, id + "F39", {"entities" : qUnion([Q0]), "radius" : 5 * mm, "tangentPropagation" : true, "allowEdgeOverflow" : false});
        }
        {
            var Q0;
            Q0=makeQuery(id+"F34.opExtrude","CAP_EDGE",EDGE,{"disambiguationData":[OSD([sQuery(id+"F33.wireOp",EDGE,"E68.top")])],"isStart":false});
            fillet(context, id + "F40", {"entities" : qUnion([Q0]), "radius" : 2 * mm, "tangentPropagation" : true, "allowEdgeOverflow" : false});
        }
        {
            var Q0;
            Q0=makeQuery(id+"F36.boolean.opBoolean","COPY",EDGE,{"derivedFrom":makeQuery(id+"F36.opExtrude","CAP_EDGE",EDGE,{"disambiguationData":[OSD([sQuery(id+"F35.wireOp",EDGE,"E69.bottom")])],"isStart":false})});
            fillet(context, id + "F41", {"entities" : qUnion([Q0]), "radius" : 2 * mm, "tangentPropagation" : true, "allowEdgeOverflow" : false});
        }
        {
            var Q0;
            Q0=makeQuery(id+"F34.opExtrude","CAP_FACE",FACE,{"disambiguationData":[OSD([sQuery(id+"F33.wireOp",EDGE,"E68.bottom"),sQuery(id+"F33.wireOp",EDGE,"E68.top"),sQuery(id+"F33.wireOp",EDGE,"E68.left"),sQuery(id+"F33.wireOp",EDGE,"E68.right")])],"isStart":false});
            var sketch = newSketch(context, id + "F42", { "sketchPlane" : qUnion([Q0])});
            skLineSegment(sketch, "E72.bottom", {"start": v(-319.1, 108.87) * mm, "end": v(-163.1, 108.87) * mm, "construction": true});
            skLineSegment(sketch, "E72.top", {"start": v(-319.1, -42.13) * mm, "end": v(-163.1, -42.13) * mm, "construction": true});
            skLineSegment(sketch, "E72.left", {"start": v(-319.1, 108.87) * mm, "end": v(-319.1, -42.13) * mm, "construction": true});
            skLineSegment(sketch, "E72.right", {"start": v(-163.1, 108.87) * mm, "end": v(-163.1, -42.13) * mm, "construction": true});
            skLineSegment(sketch, "E73", {"start": v(-241.1, 108.87) * mm, "end": v(-241.1, 118.87) * mm, "construction": true});
            skLineSegment(sketch, "E74", {"start": v(-163.1, 33.37) * mm, "end": v(-179.1, 33.37) * mm, "construction": true});
            skCircle(sketch, "E75", {"center": v(-319.1, 108.87) * mm, "radius": 3.24 * mm});
            skCircle(sketch, "E76", {"center": v(-241.1, 108.87) * mm, "radius": 3.24 * mm});
            skCircle(sketch, "E77", {"center": v(-163.1, 108.87) * mm, "radius": 3.24 * mm});
            skCircle(sketch, "E78", {"center": v(-163.1, 33.37) * mm, "radius": 3.24 * mm});
            skCircle(sketch, "E79", {"center": v(-163.1, -42.13) * mm, "radius": 3.24 * mm});
            skCircle(sketch, "E80", {"center": v(-319.1, -42.13) * mm, "radius": 3.24 * mm});
            skCircle(sketch, "E81", {"center": v(-241.1, -42.13) * mm, "radius": 3.24 * mm});
            skCircle(sketch, "E82", {"center": v(-319.1, 33.37) * mm, "radius": 3.24 * mm});
            skSolve(sketch);
        }
        {
            var Q0;
            Q0 = qSketchRegion(id + "F42", true);
            extrude(context, id + "F43", {"entities" : qUnion([Q0]), "operationType" : NewBodyOperationType.REMOVE, "endBound" : BoundingType.THROUGH_ALL, "oppositeDirection" : true, "depth" : 25 * mm});
        }
        {
            var Q0;
            Q0=makeQuery(id+"F1.opExtrude","SWEPT_FACE",FACE,{"disambiguationData":[OSD([sQuery(id+"F0.wireOp",EDGE,"E0.left")])]});
            var sketch = newSketch(context, id + "F44", { "sketchPlane" : qUnion([Q0])});
            skCircle(sketch, "E83", {"center": v(52.5, 12) * mm, "radius": 5 * mm});
            skCircle(sketch, "E84", {"center": v(34.5, 12) * mm, "radius": 5 * mm});
            skCircle(sketch, "E85", {"center": v(16.5, 12) * mm, "radius": 5 * mm});
            skSolve(sketch);
        }
        {
            var Q0;
            Q0 = qSketchRegion(id + "F44", true);
            var Q1;
            Q1=makeQuery(id+"F4.boolean.opBoolean","COPY",FACE,{"derivedFrom":makeQuery(id+"F4.opExtrude","SWEPT_FACE",FACE,{"disambiguationData":[OSD([sQuery(id+"F3.wireOp",EDGE,"E3.left")])]})});
            extrude(context, id + "F45", {"entities" : qUnion([Q0]), "operationType" : NewBodyOperationType.REMOVE, "endBound" : BoundingType.UP_TO_SURFACE, "oppositeDirection" : true, "endBoundEntityFace" : qUnion([Q1]), "depth" : 25 * mm});
        }
        {
            var Q0;
            Q0=makeQuery(id+"F34.opExtrude","SWEPT_FACE",FACE,{"disambiguationData":[OSD([sQuery(id+"F33.wireOp",EDGE,"E68.left")])]});
            var sketch = newSketch(context, id + "F46", { "sketchPlane" : qUnion([Q0])});
            skCircle(sketch, "E86", {"center": v(-49.87, 32) * mm, "radius": 5 * mm});
            skCircle(sketch, "E87", {"center": v(-67.87, 32) * mm, "radius": 5 * mm});
            skCircle(sketch, "E88", {"center": v(-85.87, 32) * mm, "radius": 5 * mm});
            skSolve(sketch);
        }
        {
            var Q0;
            Q0 = qSketchRegion(id + "F46", true);
            extrude(context, id + "F47", {"entities" : qUnion([Q0]), "operationType" : NewBodyOperationType.REMOVE, "oppositeDirection" : true, "depth" : 32 * mm});
        }
    });
